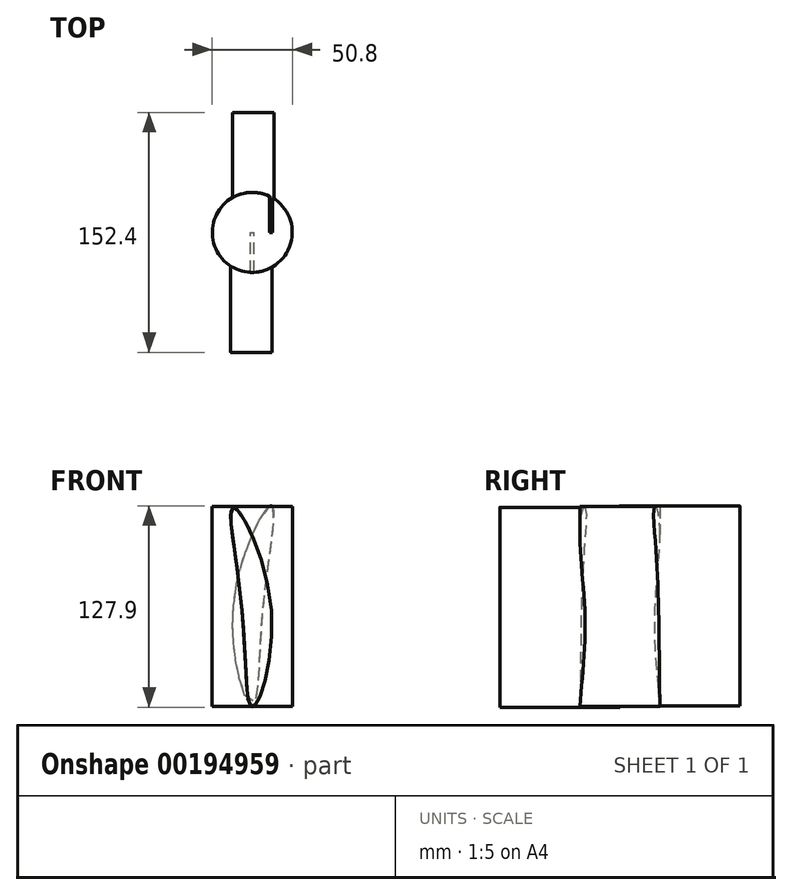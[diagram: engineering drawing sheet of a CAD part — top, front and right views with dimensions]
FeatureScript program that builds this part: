
annotation { "Feature Type Name" : "Feature", "Feature Type Description" : "" }
export const myFeature = defineFeature(function(context is Context, id is Id, definition is map)
    precondition{}
    {
        {
            var Q0;
            Q0=qCreatedBy(makeId("Top.planeOp"),FACE);
            var sketch = newSketch(context, id + "F0", { "sketchPlane" : qUnion([Q0])});
            skCircle(sketch, "E0", {"center": v(0, 0) * mm, "radius": 25.4 * mm});
            skSolve(sketch);
        }
        {
            var Q0;
            Q0 = qSketchRegion(id + "F0", true);
            extrude(context, id + "F1", {"entities" : qUnion([Q0]), "endBound" : BoundingType.SYMMETRIC, "depth" : 127 * mm});
        }
        {
            var Q0;
            Q0=qCreatedBy(makeId("Front.planeOp"),FACE);
            var sketch = newSketch(context, id + "F2", { "sketchPlane" : qUnion([Q0])});
            skLineSegment(sketch, "E1", {"start": v(0, 63.87) * mm, "end": v(0, -63.13) * mm, "construction": true});
            skFitSpline(sketch, "E2", {"points": [v(12.2, 63.87) * mm, v(6.66, 0) * mm, v(0, -63.13) * mm, v(-12.02, 0) * mm, v(12.2, 63.87) * mm]});
            skSolve(sketch);
        }
        {
            var Q0;
            Q0 = qSketchRegion(id + "F2", true);
            var Q1;
            Q1=sQuery(id+"F2.wireOp",EDGE,"E2");
            extrude(context, id + "F3", {"entities" : qUnion([Q0]), "operationType" : NewBodyOperationType.ADD, "surfaceEntities" : qUnion([Q1]), "oppositeDirection" : true, "depth" : 76.2 * mm});
        }
        {
            var Q0;
            Q0=qCreatedBy(makeId("Front.planeOp"),FACE);
            var sketch = newSketch(context, id + "F4", { "sketchPlane" : qUnion([Q0])});
            skLineSegment(sketch, "E3", {"start": v(-0.04, 62.98) * mm, "end": v(-0.04, -64.02) * mm, "construction": true});
            skFitSpline(sketch, "E4.MirrorC", {"points": [v(-12.25, 62.98) * mm, v(-6.7, -0.89) * mm, v(-0.04, -64.02) * mm, v(11.98, -0.89) * mm, v(-12.25, 62.98) * mm]});
            skSolve(sketch);
        }
        {
            var Q0;
            Q0 = qSketchRegion(id + "F4", true);
            var Q1;
            Q1=sQuery(id+"F4.wireOp",EDGE,"E4.MirrorC");
            extrude(context, id + "F5", {"entities" : qUnion([Q0]), "operationType" : NewBodyOperationType.ADD, "surfaceEntities" : qUnion([Q1]), "depth" : 76.2 * mm});
        }
    });
